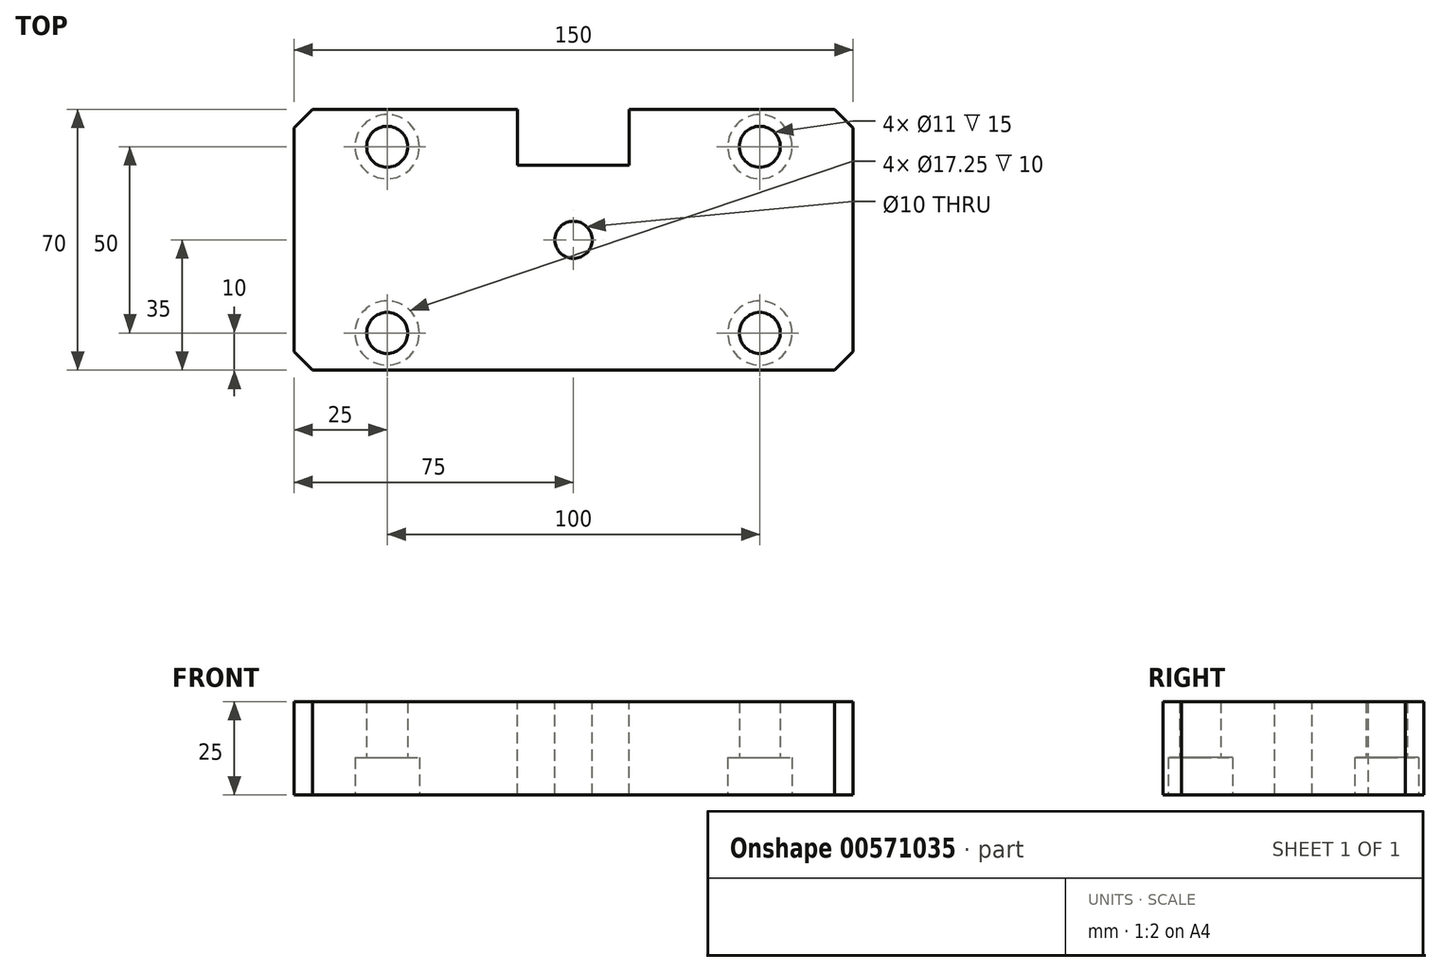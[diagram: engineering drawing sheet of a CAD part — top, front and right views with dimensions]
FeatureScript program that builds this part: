
annotation { "Feature Type Name" : "Feature", "Feature Type Description" : "" }
export const myFeature = defineFeature(function(context is Context, id is Id, definition is map)
    precondition{}
    {
        {
            var Q0;
            Q0=qCreatedBy(makeId("Top.planeOp"),FACE);
            var sketch = newSketch(context, id + "F0", { "sketchPlane" : qUnion([Q0])});
            skLineSegment(sketch, "E0.bottom", {"start": v(-75, 35) * mm, "end": v(75, 35) * mm});
            skLineSegment(sketch, "E0.top", {"start": v(-75, -35) * mm, "end": v(75, -35) * mm});
            skLineSegment(sketch, "E0.left", {"start": v(-75, 35) * mm, "end": v(-75, -35) * mm});
            skLineSegment(sketch, "E0.right", {"start": v(75, 35) * mm, "end": v(75, -35) * mm});
            skSolve(sketch);
        }
        {
            var Q0;
            Q0 = qSketchRegion(id + "F0", true);
            extrude(context, id + "F1", {"entities" : qUnion([Q0]), "depth" : 25 * mm, "offsetDistance" : 25 * mm});
        }
        {
            var Q0;
            Q0=qCreatedBy(makeId("Top.planeOp"),FACE);
            var sketch = newSketch(context, id + "F2", { "sketchPlane" : qUnion([Q0])});
            skPoint(sketch, "E1", {"position": v(-50, 25) * mm});
            skPoint(sketch, "E2", {"position": v(-50, -25) * mm});
            skPoint(sketch, "E3", {"position": v(50, -25) * mm});
            skPoint(sketch, "E4", {"position": v(50, 25) * mm});
            skSolve(sketch);
        }
        {
            var Q0;
            Q0=sQuery(id+"F2.wireOp",VERTEX,"E1");
            var Q1;
            Q1=sQuery(id+"F2.wireOp",VERTEX,"E2");
            var Q2;
            Q2=sQuery(id+"F2.wireOp",VERTEX,"E3");
            var Q3;
            Q3=sQuery(id+"F2.wireOp",VERTEX,"E4");
            var Q4;
            Q4=makeQuery(id+"F1.opExtrude","SWEPT_BODY",BODY,{"disambiguationData":[OSD([sQuery(id+"F0.wireOp",EDGE,"E0.bottom"),sQuery(id+"F0.wireOp",EDGE,"E0.top"),sQuery(id+"F0.wireOp",EDGE,"E0.left"),sQuery(id+"F0.wireOp",EDGE,"E0.right")])]});
            hole(context, id + "F3", {"style" : HoleStyle.C_BORE, "endStyle" : HoleEndStyle.THROUGH, "oppositeDirection" : true, "standardTappedOrClearance" : lookupTablePath({ "standard" : "ISO", "fit" : "Normal", "size" : "M10", "type" : "Clearance" }), "standardBlindInLast" : lookupTablePath({ "fit" : "Standard", "standard" : "ISO", "size" : "M10", "type" : "Clearance" }), "holeDiameter" : 11 * mm, "cBoreDiameter" : 17.25 * mm, "cBoreDepth" : 10 * mm, "isTappedThrough" : true, "tappedDepth" : 12 * mm, "tapClearance" : 3, "locations" : qUnion([Q0, Q1, Q2, Q3]), "scope" : qUnion([Q4])});
        }
        {
            var Q0;
            Q0=makeQuery(id+"F1.opExtrude","SWEPT_EDGE",EDGE,{"disambiguationData":[OSD([sQuery(id+"F0.wireOp",EDGE,"E0.bottom"),sQuery(id+"F0.wireOp",EDGE,"E0.left")])]});
            var Q1;
            Q1=makeQuery(id+"F1.opExtrude","SWEPT_EDGE",EDGE,{"disambiguationData":[OSD([sQuery(id+"F0.wireOp",EDGE,"E0.top"),sQuery(id+"F0.wireOp",EDGE,"E0.left")])]});
            chamfer(context, id + "F4", {"entities" : qUnion([Q0, Q1]), "width" : 5 * mm, "tangentPropagation" : true});
        }
        {
            var Q0;
            Q0=makeQuery(id+"F1.opExtrude","SWEPT_EDGE",EDGE,{"disambiguationData":[OSD([sQuery(id+"F0.wireOp",EDGE,"E0.bottom"),sQuery(id+"F0.wireOp",EDGE,"E0.right")])]});
            var Q1;
            Q1=makeQuery(id+"F1.opExtrude","SWEPT_EDGE",EDGE,{"disambiguationData":[OSD([sQuery(id+"F0.wireOp",EDGE,"E0.top"),sQuery(id+"F0.wireOp",EDGE,"E0.right")])]});
            chamfer(context, id + "F5", {"entities" : qUnion([Q0, Q1]), "width" : 5 * mm, "tangentPropagation" : true});
        }
        {
            var Q0;
            Q0=makeQuery(id+"F1.opExtrude","CAP_FACE",FACE,{"disambiguationData":[OSD([sQuery(id+"F0.wireOp",EDGE,"E0.bottom"),sQuery(id+"F0.wireOp",EDGE,"E0.top"),sQuery(id+"F0.wireOp",EDGE,"E0.left"),sQuery(id+"F0.wireOp",EDGE,"E0.right")])],"isStart":true});
            var sketch = newSketch(context, id + "F6", { "sketchPlane" : qUnion([Q0])});
            skLineSegment(sketch, "E5.bottom", {"start": v(-15, -20) * mm, "end": v(15, -20) * mm});
            skLineSegment(sketch, "E5.top", {"start": v(-15, -45) * mm, "end": v(15, -45) * mm});
            skLineSegment(sketch, "E5.left", {"start": v(-15, -20) * mm, "end": v(-15, -45) * mm});
            skLineSegment(sketch, "E5.right", {"start": v(15, -20) * mm, "end": v(15, -45) * mm});
            skSolve(sketch);
        }
        {
            var Q0;
            Q0 = qSketchRegion(id + "F6", true);
            extrude(context, id + "F7", {"entities" : qUnion([Q0]), "operationType" : NewBodyOperationType.REMOVE, "oppositeDirection" : true, "depth" : 25 * mm, "offsetDistance" : 25 * mm});
        }
        {
            var Q0;
            Q0=makeQuery(id+"F1.opExtrude","CAP_FACE",FACE,{"disambiguationData":[OSD([sQuery(id+"F0.wireOp",EDGE,"E0.bottom"),sQuery(id+"F0.wireOp",EDGE,"E0.top"),sQuery(id+"F0.wireOp",EDGE,"E0.left"),sQuery(id+"F0.wireOp",EDGE,"E0.right")])],"isStart":false});
            var sketch = newSketch(context, id + "F8", { "sketchPlane" : qUnion([Q0])});
            skPoint(sketch, "E6", {"position": v(0, 0) * mm});
            skSolve(sketch);
        }
        {
            var Q0;
            Q0=sQuery(id+"F8.wireOp",VERTEX,"E6");
            var Q1;
            Q1=makeQuery(id+"F1.opExtrude","SWEPT_BODY",BODY,{"disambiguationData":[OSD([sQuery(id+"F0.wireOp",EDGE,"E0.bottom"),sQuery(id+"F0.wireOp",EDGE,"E0.top"),sQuery(id+"F0.wireOp",EDGE,"E0.left"),sQuery(id+"F0.wireOp",EDGE,"E0.right")])]});
            hole(context, id + "F9", {"style" : HoleStyle.SIMPLE, "endStyle" : HoleEndStyle.THROUGH, "standardTappedOrClearance" : lookupTablePath({ "standard" : "ISO", "size" : "10", "type" : "Drilled" }), "standardBlindInLast" : lookupTablePath({ "standard" : "ISO", "size" : "10", "type" : "Drilled" }), "holeDiameter" : 10 * mm, "isTappedThrough" : true, "tappedDepth" : 12 * mm, "tapClearance" : 3, "locations" : qUnion([Q0]), "scope" : qUnion([Q1])});
        }
    });
